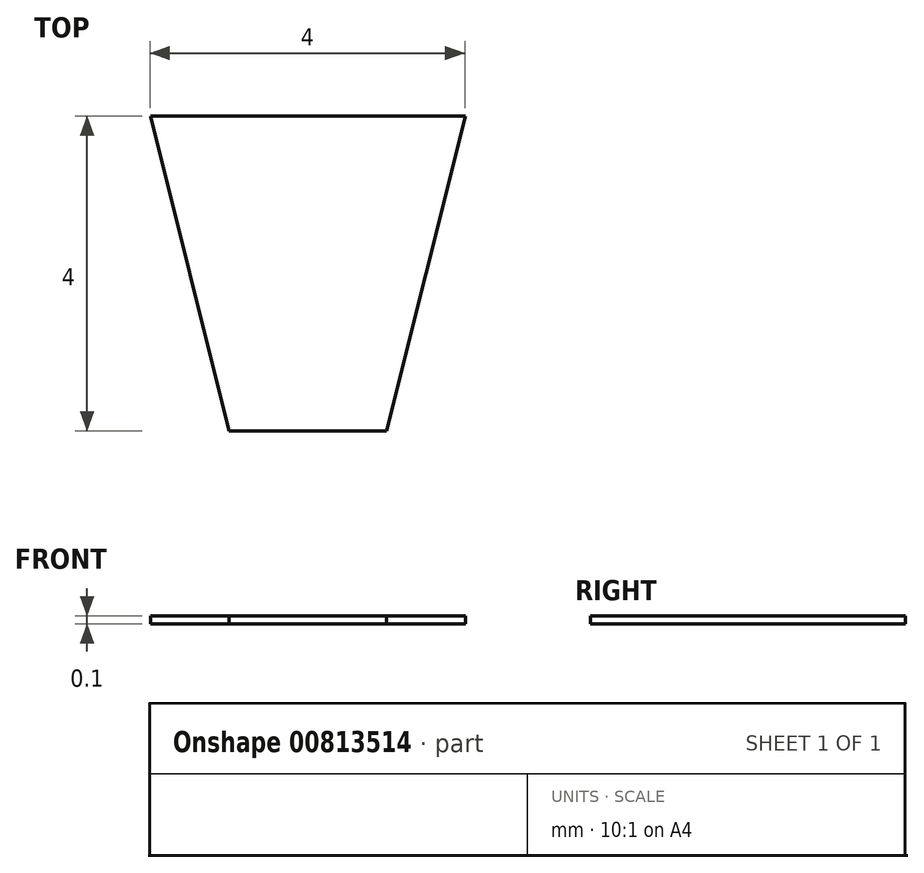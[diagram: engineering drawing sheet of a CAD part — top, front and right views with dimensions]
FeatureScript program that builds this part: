
annotation { "Feature Type Name" : "Feature", "Feature Type Description" : "" }
export const myFeature = defineFeature(function(context is Context, id is Id, definition is map)
    precondition{}
    {
        {
            var Q0;
            Q0=qCreatedBy(makeId("Top.planeOp"),FACE);
            var sketch = newSketch(context, id + "F0", { "sketchPlane" : qUnion([Q0])});
            skLineSegment(sketch, "E0.bottom", {"start": v(4.31, -9.44) * mm, "end": v(8.31, -9.44) * mm});
            skLineSegment(sketch, "E0.top", {"start": v(5.31, -13.44) * mm, "end": v(7.31, -13.44) * mm});
            skLineSegment(sketch, "E1", {"start": v(6.31, -9.44) * mm, "end": v(6.31, -13.44) * mm});
            skLineSegment(sketch, "E2", {"start": v(6.31, -13.44) * mm, "end": v(7.31, -13.44) * mm});
            skLineSegment(sketch, "E3", {"start": v(8.31, -9.44) * mm, "end": v(7.31, -13.44) * mm});
            skLineSegment(sketch, "E4.MirrorCS", {"start": v(4.31, -9.44) * mm, "end": v(5.31, -13.44) * mm});
            skPoint(sketch, "E5.orphan", {"position": v(8.31, -13.44) * mm});
            skPoint(sketch, "E6.orphan", {"position": v(4.31, -13.44) * mm});
            skSolve(sketch);
        }
        {
            var Q0;
            Q0 = qSketchRegion(id + "F0", true);
            extrude(context, id + "F1", {"entities" : qUnion([Q0]), "depth" : 0.1 * mm, "offsetDistance" : 25 * mm});
        }
    });
